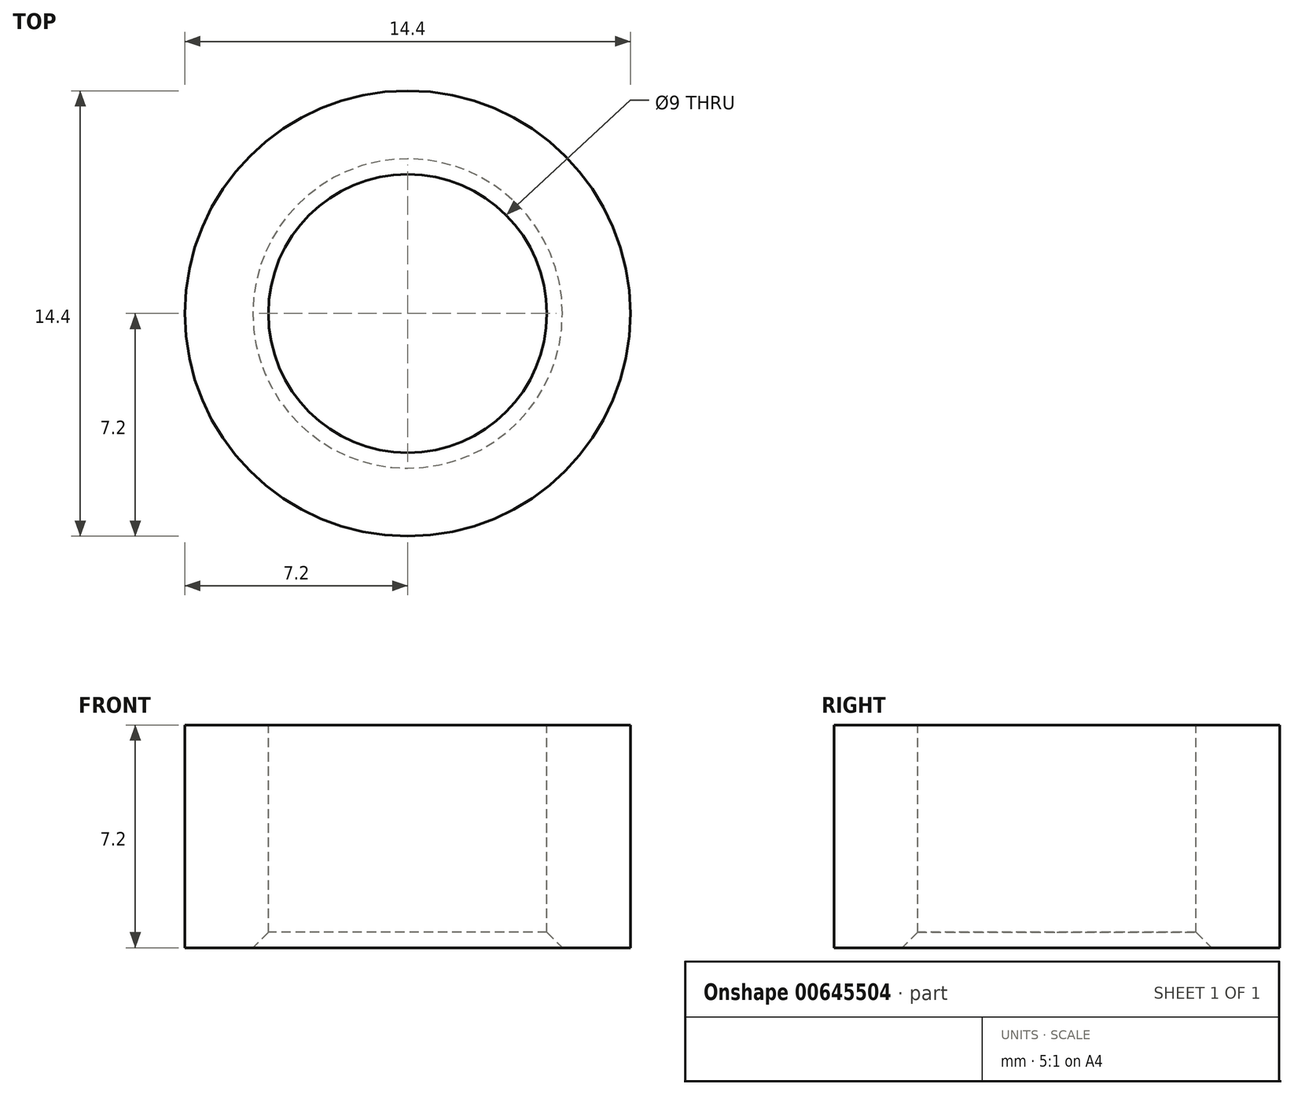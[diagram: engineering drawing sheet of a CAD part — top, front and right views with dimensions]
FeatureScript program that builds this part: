
annotation { "Feature Type Name" : "Feature", "Feature Type Description" : "" }
export const myFeature = defineFeature(function(context is Context, id is Id, definition is map)
    precondition{}
    {
        {
            var Q0;
            Q0=qCreatedBy(makeId("Top.planeOp"),FACE);
            var sketch = newSketch(context, id + "F0", { "sketchPlane" : qUnion([Q0])});
            skCircle(sketch, "E0", {"center": v(0, 0) * mm, "radius": 7.2 * mm});
            skSolve(sketch);
        }
        {
            var Q0;
            Q0=makeQuery(id+"F0.imprint","IMPRINT",FACE,{"disambiguationData":[TD([[makeQuery(id+"F0.imprint","IMPRINT",EDGE,{"derivedFrom":sQuery(id+"F0.wireOp",EDGE,"E0")}),1.0]])]});
            extrude(context, id + "F1", {"entities" : qUnion([Q0]), "depth" : 7.2 * mm, "offsetDistance" : 25 * mm});
        }
        {
            var Q0;
            Q0=makeQuery(id+"F1.opExtrude","CAP_FACE",FACE,{"disambiguationData":[OSD([sQuery(id+"F0.wireOp",EDGE,"E0")])],"isStart":false});
            var sketch = newSketch(context, id + "F2", { "sketchPlane" : qUnion([Q0])});
            skCircle(sketch, "E1", {"center": v(0, 0) * mm, "radius": 4.5 * mm});
            skSolve(sketch);
        }
        {
            var Q0;
            Q0=makeQuery(id+"F2.imprint","IMPRINT",FACE,{"disambiguationData":[TD([[makeQuery(id+"F2.imprint","IMPRINT",EDGE,{"derivedFrom":sQuery(id+"F2.wireOp",EDGE,"E1")}),1.0]])]});
            extrude(context, id + "F3", {"entities" : qUnion([Q0]), "operationType" : NewBodyOperationType.REMOVE, "endBound" : BoundingType.THROUGH_ALL, "oppositeDirection" : true, "depth" : 25 * mm, "offsetDistance" : 25 * mm});
        }
        {
            var Q0;
            Q0=makeQuery(id+"F3.boolean.opBoolean","COPY",EDGE,{"derivedFrom":makeQuery(id+"F3.opExtrude","CAP_EDGE",EDGE,{"disambiguationData":[OSD([sQuery(id+"F2.wireOp",EDGE,"E1")])],"isStart":true})});
            var Q1;
            Q1=makeQuery(id+"F3.boolean.opBoolean","INTERSECT",EDGE,{"derivedFrom":[makeQuery(id+"F1.opExtrude","CAP_FACE",FACE,{"disambiguationData":[OSD([sQuery(id+"F0.wireOp",EDGE,"E0")])],"isStart":true}),makeQuery(id+"F3.opExtrude","SWEPT_FACE",FACE,{"disambiguationData":[OSD([sQuery(id+"F2.wireOp",EDGE,"E1")])]})]});
            chamfer(context, id + "F4", {"entities" : qUnion([Q0, Q1]), "width" : 0.5 * mm, "tangentPropagation" : true});
        }
    });
